# Revit family: Table-LAMMHULTS-QUICKLY-T_Leg
name_source: partatom
category: Furniture
revit_build: Autodesk Revit Architecture 2012 (Build: 20110916_2132(x64)
units: mm (PartAtom-declared; Revit-internal decimal feet)

## types (13) — shared parameters
Assembly Code = E2020
Description = *Please enter mtrl description here for use in mto*
Frame Material = Plastic - White
Keynote = 46.B
Legs Material = Metal - Chrome - Polished
Manufacturer = LAMMHULTS
Model = QUICKLY
URL = www.lammhults.se

## per-type parameters (varying)
| type | Frame Distance | Leg Distance | Leg Height | Table Top Lenght | Table Top Material | Table Top Width |
| 120x50 Birch Veneer | 115 mm  [stored 0.377297 ft] | 515 mm  [stored 1.68963 ft] | 98 mm  [stored 0.321522 ft] | 1200 mm  [stored 3.93701 ft] | Wood - Veneer - Birch | 500 mm  [stored 1.64042 ft] |
| 120x60 Birch Veneer | 140 mm | 515 mm  [stored 1.68963 ft] | 116 mm | 1200 mm  [stored 3.93701 ft] | Wood - Veneer - Birch | 600 mm |
| 120x70 Birch Veneer | 190 mm | 515 mm  [stored 1.68963 ft] | 134 mm | 1200 mm  [stored 3.93701 ft] | Wood - Veneer - Birch | 700 mm  [stored 2.29659 ft] |
| 120x75 Birch Veneer | 190 mm | 515 mm  [stored 1.68963 ft] | 134 mm | 1200 mm  [stored 3.93701 ft] | Wood - Veneer - Birch | 750 mm |
| 120x80 Birch Veneer | 240 mm | 515 mm  [stored 1.68963 ft] | 152 mm | 1200 mm  [stored 3.93701 ft] | Wood - Veneer - Birch | 800 mm |
| 140x50 Laminate | 115 mm  [stored 0.377297 ft] | 615 mm | 98 mm  [stored 0.321522 ft] | 1400 mm | Laminate - High Pressure - White/Grey | 500 mm  [stored 1.64042 ft] |
| 140x60 Birch Veneer | 140 mm | 615 mm | 116 mm | 1400 mm | Wood - Veneer - Birch | 600 mm |
| 140x70 Birch Veneer | 190 mm | 615 mm | 134 mm | 1400 mm | Wood - Veneer - Birch | 700 mm  [stored 2.29659 ft] |
| 140x75 Birch Veneer | 190 mm | 615 mm | 134 mm | 1400 mm | Wood - Veneer - Birch | 750 mm |
| 140x80 Birch Veneer | 240 mm | 615 mm | 152 mm | 1400 mm | Wood - Veneer - Birch | 800 mm |
| 180x60 Birch Veneer | 140 mm | 815 mm | 116 mm | 1800 mm | Wood - Veneer - Birch | 600 mm |
| 180x70 Birch Veneer | 190 mm | 815 mm | 134 mm | 1800 mm | Wood - Veneer - Birch | 700 mm  [stored 2.29659 ft] |
| 180x75 Birch Veneer | 190 mm | 815 mm | 134 mm | 1800 mm | Wood - Veneer - Birch | 750 mm |

note: [stored X ft] marks values corroborated as IEEE doubles in the binary element streams (Revit-internal decimal feet)

## geometry (parser evidence)
native form markers: Blend x10, Sweep x2
no freeform markers — native parametric forms only
